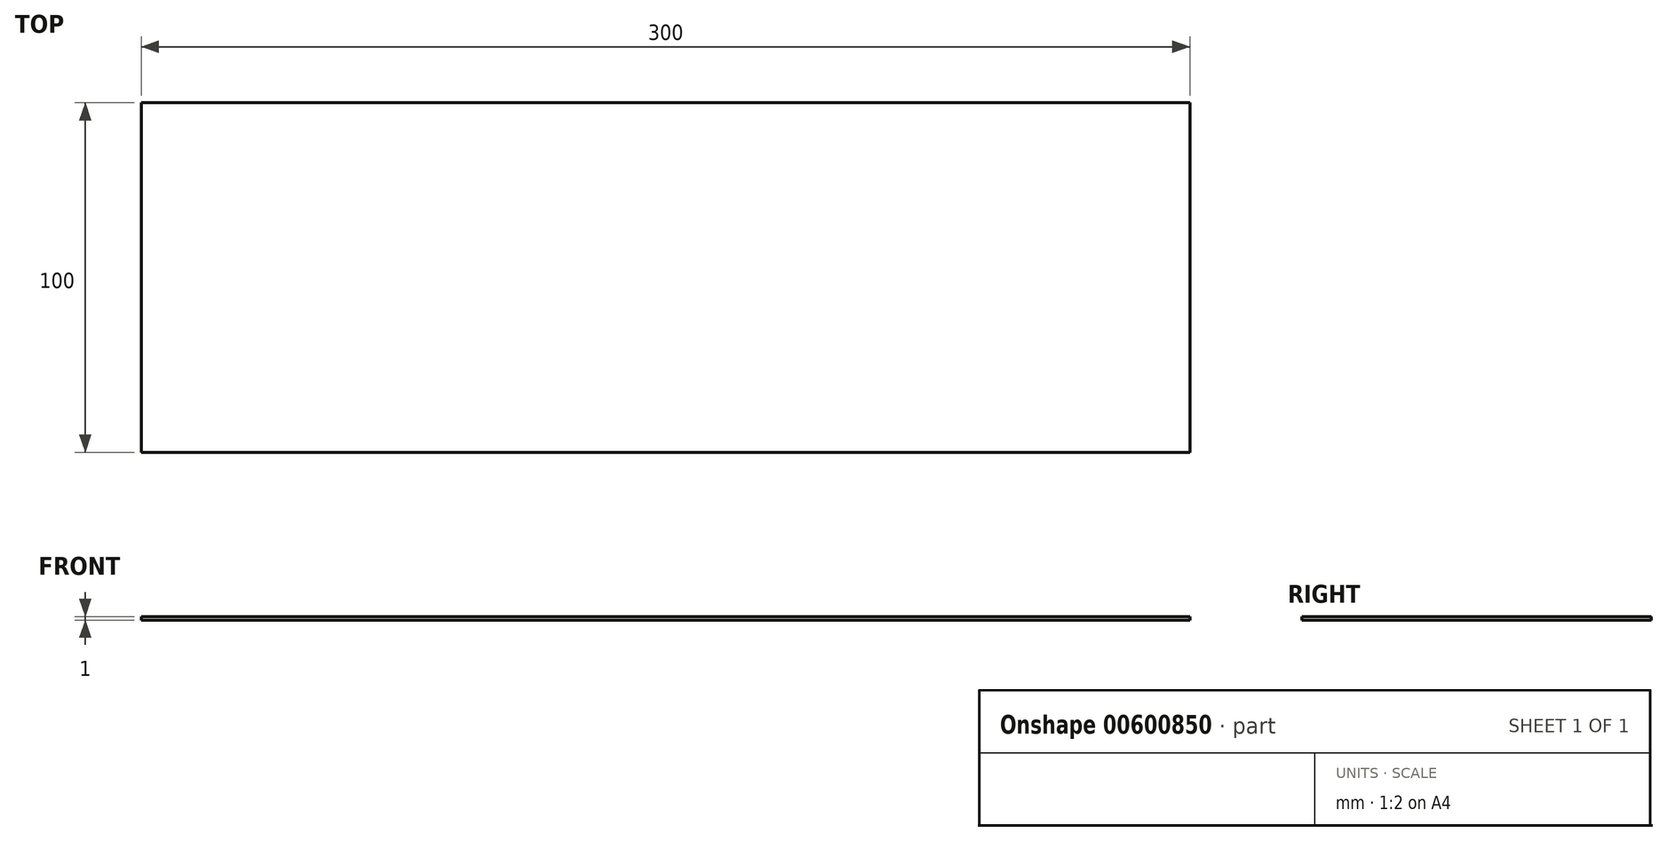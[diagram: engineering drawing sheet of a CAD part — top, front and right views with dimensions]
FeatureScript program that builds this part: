
annotation { "Feature Type Name" : "Feature", "Feature Type Description" : "" }
export const myFeature = defineFeature(function(context is Context, id is Id, definition is map)
    precondition{}
    {
        {
            var Q0;
            Q0=qCreatedBy(makeId("Top.planeOp"),FACE);
            var sketch = newSketch(context, id + "F0", { "sketchPlane" : qUnion([Q0])});
            skLineSegment(sketch, "E0.bottom", {"start": v(-150, 50) * mm, "end": v(150, 50) * mm});
            skLineSegment(sketch, "E0.top", {"start": v(-150, -50) * mm, "end": v(150, -50) * mm});
            skLineSegment(sketch, "E0.left", {"start": v(-150, 50) * mm, "end": v(-150, -50) * mm});
            skLineSegment(sketch, "E0.right", {"start": v(150, 50) * mm, "end": v(150, -50) * mm});
            skLineSegment(sketch, "E1", {"start": v(0, 50) * mm, "end": v(0, -50) * mm});
            skSolve(sketch);
        }
        {
            var Q0;
            {var subQ0=sQuery(id+"F0.wireOp",EDGE,"E0.left");Q0=makeQuery(id+"F0.imprint","IMPRINT",FACE,{"disambiguationData":[TD([[makeQuery(id+"F0.imprint","IMPRINT",EDGE,{"derivedFrom":subQ0}),1.0]])]});}
            var Q1;
            {var subQ0=sQuery(id+"F0.wireOp",EDGE,"E0.right");Q1=makeQuery(id+"F0.imprint","IMPRINT",FACE,{"disambiguationData":[TD([[makeQuery(id+"F0.imprint","IMPRINT",EDGE,{"derivedFrom":subQ0}),-1.0]])]});}
            extrude(context, id + "F1", {"entities" : qUnion([Q0, Q1]), "depth" : 1 * mm, "offsetDistance" : 25 * mm});
        }
    });
